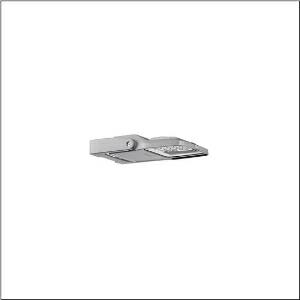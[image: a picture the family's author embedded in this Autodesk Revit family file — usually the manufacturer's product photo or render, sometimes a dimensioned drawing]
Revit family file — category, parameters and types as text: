
# Revit family: floodlight_fl_21_iq_micro___pl52_5xa7762a2d2a_5d06
name_source: partatom
category: Lighting Fixtures
units: mm (PartAtom-declared; Revit-internal decimal feet)

## family parameters
Cut with Voids When Loaded = No
Host = Face
Light Source = No
Part Type = Normal
Room Calculation Point = No
Round Connector Dimension = Use Diameter
Shared = No

## types (1)
- --- (1 x LED, 2890 lm, 23.1 W, 3000K)
    Apparent Load = 23 VA
    CIE Flux Codes = 26 60 98 100 100
    Color Rendering = 70
    Color Temperature = 3000K
    Default Elevation = 1800 mm
    Description = Floodlight FL 21 iQ micro, floodlight, primary light control with lens, of PMMA, primary optical cover: protective disc, of toughened safety glass, transparent, light distribution: PL52, light emission: direct distribution, installation type: surface-mounted, LED, High Power LED, rated luminous flux: 2.890lm, luminous efficacy: 125lm/W, light colour: 730, colour temperature: 3000K, control gear: iQ Street-Remote/DALI, control: Auto-Match, Temp-Guard, Night-Set, Smart-Wire, Desk-Remote (wireless, voltage-free reading and setting of iQ features in the workshop via application-optimized NFC function/RFID function), optimised constant luminous flux control (CLO 2.0), Street-Remote, with terminal, 6-pole, mains connection: 220..240V, AC, 50/60Hz, start of lifetime: 23W, end of service life: 24W, reduction: 11W, luminaire housing, of diecast aluminium, powder-coated, Siteco® metallic grey (DB 702S), corrosivity category C5 mid according to DIN EN ISO 12944, suitable for swimming pools, chlorine-resistant, sealing non-destructively replaceable, design bracket, of diecast aluminium, powder-coated, Siteco® metallic grey (DB 702S), protection rating (complete): IP66, insulation class (complete): insulation class II (safety insulation), certification: CE, ENEC, VDE, protection symbol: D, impact resistance: IK07, permissible operating ambient temperature: -40..+40°C, permissible operating ambient temperature for outdoor applications: -40..+50°C, standard: DIN EN 12944, LABS conformity tested according to VDMA 24364:2018-05, packaging unit: 1 piece

Light Distribution: PL52
    Height = 65 mm
    Lamp = 1 x LED
    Lamp Light Flux = 2890 lm
    Lamp Power = 23.1 W
    Lamp count = 1
    Length = 312 mm
    Luminous efficacy = 125 lm/W
    Manufacturer = Siteco
    ModVariant = No
    Model = 5XA7762A2D2A
    Mounting Place = Wall
    Mounting Type = Surface mounted
    Number of Poles = 1
    OnlyDefault = Yes
    Power Factor = 1
    Product Name = Floodlight FL 21 iQ micro | PL52
    Product group = floodlight | wall mounted
    ProductGroupID = 2001
    Protection Class = Protection class II
    Protection Degree = IP 66
    RLX_Detail_Level = 1
    RLX_Emergency_Light_Flux = 0 lm
    RLX_Emergency_Type = 0
    RLX_Emergency_Type_DB = No
    RlxData = <blob elided: 97637 chars, md5=c1042f8b>
    Socket = socket
    Standby Power = 0 W
    System Light Flux = 2890 lm
    System Power = 23 W
    Type Comments = factory setting: luminous flux: 100 % | dim-lin: 254 | 455 mA
    Type Image = l_1006878.jpg
    URL = http://relux.com
    VarID = @adj_177882
    Voltage = 0 V
    Weight = 0.00 kg
    Width = 230 mm

## geometry (parser evidence)
native form markers: Blend x4, Sweep x14
no freeform markers — native parametric forms only
